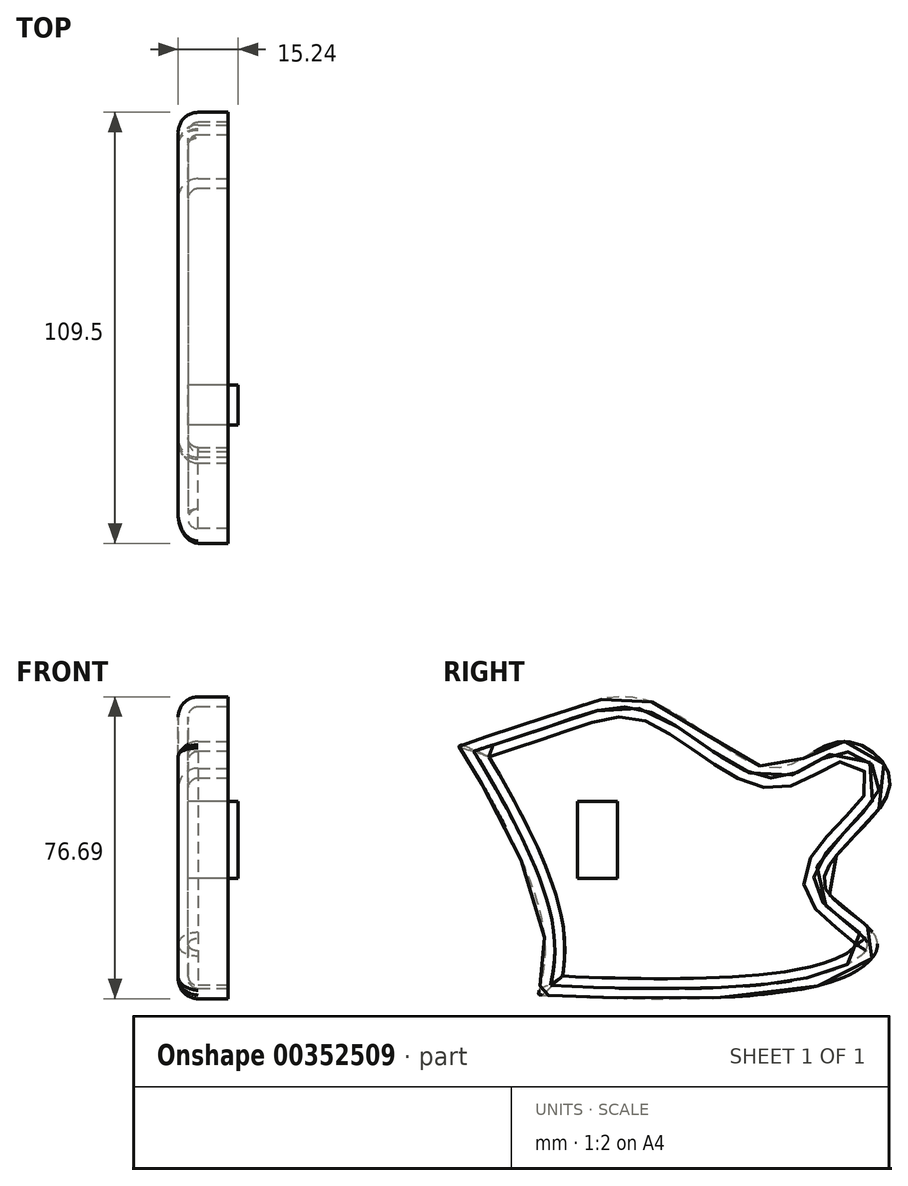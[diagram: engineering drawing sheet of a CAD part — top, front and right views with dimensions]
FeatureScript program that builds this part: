
annotation { "Feature Type Name" : "Feature", "Feature Type Description" : "" }
export const myFeature = defineFeature(function(context is Context, id is Id, definition is map)
    precondition{}
    {
        {
            var Q0;
            Q0=qCreatedBy(makeId("Right.planeOp"),FACE);
            var sketch = newSketch(context, id + "F0", { "sketchPlane" : qUnion([Q0])});
            skFitSpline(sketch, "E0", {"points": [v(-47.7, 31.38) * mm, v(-20.73, 35.07) * mm, v(9.94, 18.31) * mm, v(27.54, 25.13) * mm, v(39.47, 13.49) * mm, v(22.71, -10.36) * mm, v(35.78, -24.28) * mm, v(21.86, -36.77) * mm, v(-48.84, -39.33) * mm, v(-49.69, -39.04) * mm, v(-48.84, -20.59) * mm, v(-69.85, 23.7) * mm, v(-69.85, 24) * mm, v(-47.7, 31.38) * mm]});
            skSolve(sketch);
        }
        {
            var Q0;
            Q0 = qSketchRegion(id + "F0", true);
            extrude(context, id + "F1", {"entities" : qUnion([Q0]), "endBound" : BoundingType.SYMMETRIC, "depth" : 12.7 * mm});
        }
        {
            var Q0;
            Q0=makeQuery(id+"F1.opExtrude","CAP_EDGE",EDGE,{"disambiguationData":[OSD([sQuery(id+"F0.wireOp",EDGE,"E0")])],"isStart":true});
            fillet(context, id + "F2", {"entities" : qUnion([Q0]), "radius" : 5.08 * mm, "tangentPropagation" : true, "allowEdgeOverflow" : false});
        }
        {
            var Q0;
            Q0=makeQuery(id+"F1.opExtrude","CAP_FACE",FACE,{"disambiguationData":[OSD([sQuery(id+"F0.wireOp",EDGE,"E0")])],"isStart":false});
            shell(context, id + "F3", {"entities" : qUnion([Q0]), "thickness" : 2.54 * mm});
        }
        {
            var Q0;
            {var subQ0=sQuery(id+"F0.wireOp",EDGE,"E0");Q0=makeQuery(id+"F3.opShell","OFFSET_FACE",FACE,{"disambiguationData":[OSD([subQ0]),TDD([makeQuery(id+"F1.opExtrude","CAP_FACE",FACE,{"disambiguationData":[OSD([subQ0])],"isStart":true})])]});}
            var sketch = newSketch(context, id + "F4", { "sketchPlane" : qUnion([Q0])});
            skLineSegment(sketch, "E1.bottom", {"start": v(-39.84, -9.62) * mm, "end": v(-29.73, -9.62) * mm});
            skLineSegment(sketch, "E1.top", {"start": v(-39.84, 9.84) * mm, "end": v(-29.73, 9.84) * mm});
            skLineSegment(sketch, "E1.left", {"start": v(-39.84, -9.62) * mm, "end": v(-39.84, 9.84) * mm});
            skLineSegment(sketch, "E1.right", {"start": v(-29.73, -9.62) * mm, "end": v(-29.73, 9.84) * mm});
            skSolve(sketch);
        }
        {
            var Q0;
            Q0=makeQuery(id+"F4.imprint","IMPRINT",FACE,{"disambiguationData":[TD([[makeQuery(id+"F4.imprint","IMPRINT",EDGE,{"derivedFrom":sQuery(id+"F4.wireOp",EDGE,"E1.bottom")}),1.0]])]});
            extrude(context, id + "F5", {"entities" : qUnion([Q0]), "operationType" : NewBodyOperationType.ADD, "depth" : 12.7 * mm});
        }
    });
